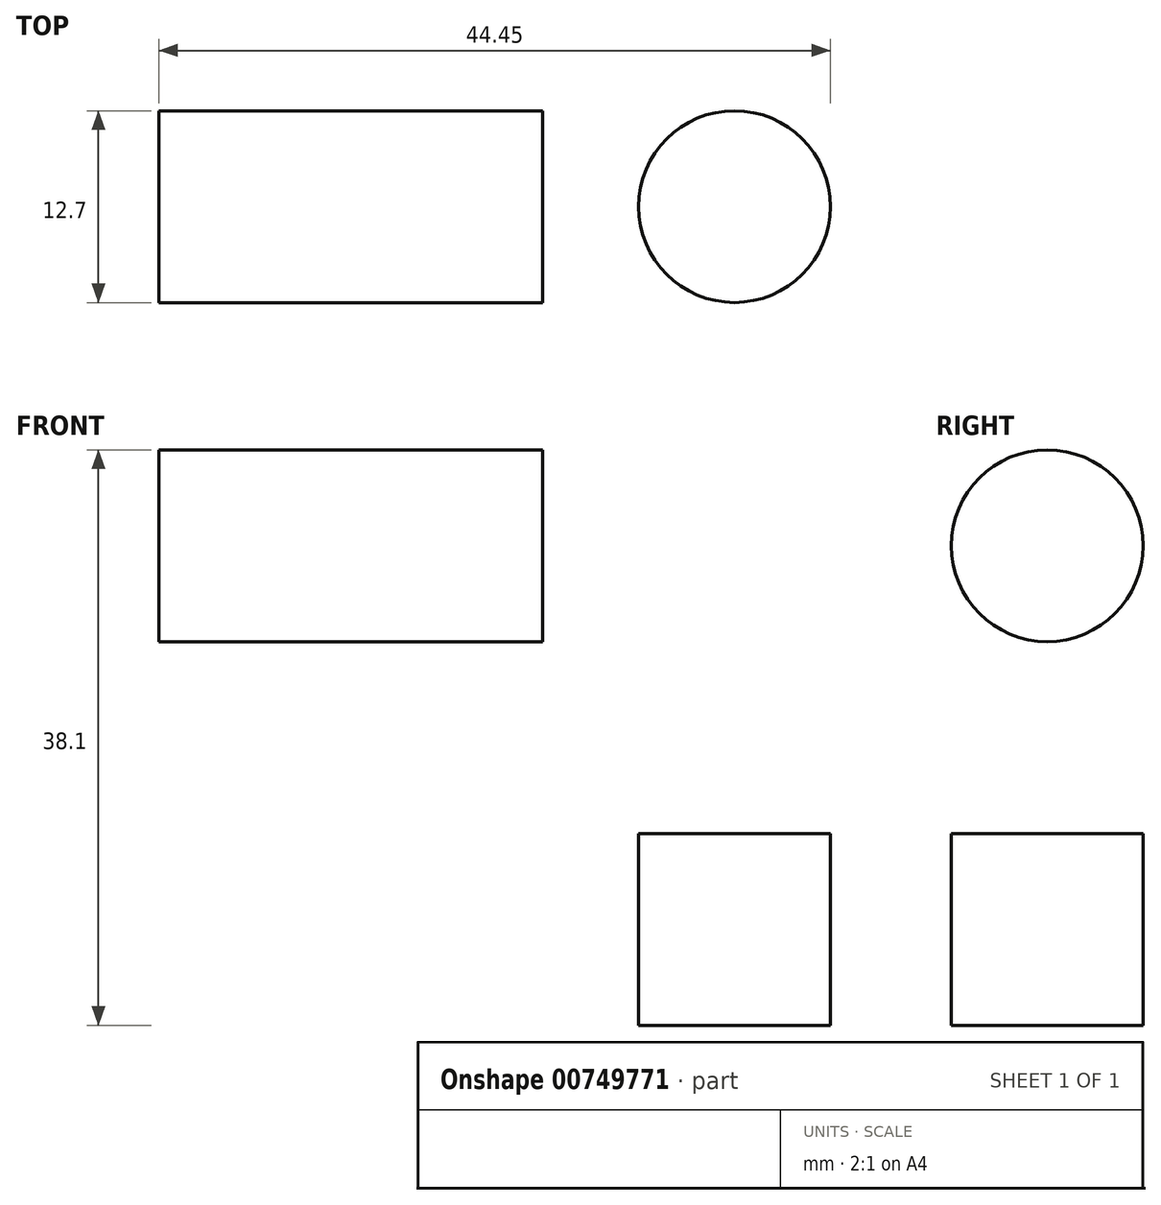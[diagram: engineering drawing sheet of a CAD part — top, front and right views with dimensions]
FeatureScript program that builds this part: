
annotation { "Feature Type Name" : "Feature", "Feature Type Description" : "" }
export const myFeature = defineFeature(function(context is Context, id is Id, definition is map)
    precondition{}
    {
        {
            var Q0;
            Q0=qCreatedBy(makeId("Front.planeOp"),FACE);
            var sketch = newSketch(context, id + "F0", { "sketchPlane" : qUnion([Q0])});
            skLineSegment(sketch, "E0", {"start": v(0, 0) * mm, "end": v(76.2, 0) * mm});
            skLineSegment(sketch, "E1", {"start": v(76.2, 0) * mm, "end": v(76.2, 12.7) * mm});
            skLineSegment(sketch, "E2", {"start": v(76.2, 12.7) * mm, "end": v(50.8, 12.7) * mm});
            skLineSegment(sketch, "E3", {"start": v(50.8, 12.7) * mm, "end": v(50.8, 44.45) * mm});
            skLineSegment(sketch, "E4", {"start": v(50.8, 44.45) * mm, "end": v(25.4, 44.45) * mm});
            skLineSegment(sketch, "E5", {"start": v(25.4, 44.45) * mm, "end": v(25.4, 12.7) * mm});
            skLineSegment(sketch, "E6", {"start": v(25.4, 12.7) * mm, "end": v(0, 12.7) * mm});
            skLineSegment(sketch, "E7", {"start": v(0, 12.7) * mm, "end": v(0, 0) * mm});
            skSolve(sketch);
        }
        {
            var Q0;
            Q0 = qSketchRegion(id + "F0", true);
            extrude(context, id + "F1", {"entities" : qUnion([Q0]), "depth" : 25.4 * mm, "offsetDistance" : 25.4 * mm});
        }
        {
            var Q0;
            Q0=makeQuery(id+"F1.opExtrude","SWEPT_FACE",FACE,{"disambiguationData":[OSD([sQuery(id+"F0.wireOp",EDGE,"E3")])]});
            var sketch = newSketch(context, id + "F2", { "sketchPlane" : qUnion([Q0])});
            skLineSegment(sketch, "E8", {"start": v(-25.4, 31.75) * mm, "end": v(0, 31.75) * mm});
            skCircle(sketch, "E9", {"center": v(-12.7, 31.75) * mm, "radius": 6.35 * mm});
            skArc(sketch, "E10", {"start": v(0, 31.75) * mm, "mid": v(-12.7, 44.42) * mm, "end": v(-25.4, 31.75) * mm});
            skSolve(sketch);
        }
        {
            var Q0;
            {var subQ0=sQuery(id+"F2.wireOp",EDGE,"E9");var subQ1=sQuery(id+"F2.wireOp",EDGE,"E8");var subQ2=makeQuery(id+"F2.imprint","INTERSECT",VERTEX,{"disambiguationData":[OD(0.0)],"derivedFrom":[subQ1,subQ0]});Q0=makeQuery(id+"F2.imprint","IMPRINT",FACE,{"disambiguationData":[TD([[makeQuery(id+"F2.imprint","IMPRINT",EDGE,{"disambiguationData":[TD([[subQ2,-1.0]])],"derivedFrom":subQ1}),-1.0]])]});}
            var Q1;
            {var subQ0=sQuery(id+"F2.wireOp",EDGE,"E9");var subQ1=sQuery(id+"F2.wireOp",EDGE,"E8");var subQ2=makeQuery(id+"F2.imprint","INTERSECT",VERTEX,{"disambiguationData":[OD(0.0)],"derivedFrom":[subQ1,subQ0]});Q1=makeQuery(id+"F2.imprint","IMPRINT",FACE,{"disambiguationData":[TD([[makeQuery(id+"F2.imprint","IMPRINT",EDGE,{"disambiguationData":[TD([[subQ2,-1.0]])],"derivedFrom":subQ1}),1.0]])]});}
            var Q2;
            {var subQ0=sQuery(id+"F2.wireOp",EDGE,"E10");Q2=makeQuery(id+"F2.imprint","IMPRINT",FACE,{"disambiguationData":[TD([[makeQuery(id+"F2.imprint","IMPRINT",EDGE,{"derivedFrom":subQ0}),-1.0]])]});}
            extrude(context, id + "F3", {"entities" : qUnion([Q0, Q1, Q2]), "operationType" : NewBodyOperationType.REMOVE, "endBound" : BoundingType.THROUGH_ALL, "oppositeDirection" : true, "depth" : 25.4 * mm, "offsetDistance" : 25.4 * mm});
        }
        {
            var Q0;
            Q0=makeQuery(id+"F1.opExtrude","SWEPT_FACE",FACE,{"disambiguationData":[OSD([sQuery(id+"F0.wireOp",EDGE,"E2")])]});
            var sketch = newSketch(context, id + "F4", { "sketchPlane" : qUnion([Q0])});
            skLineSegment(sketch, "E11", {"start": v(63.5, 0) * mm, "end": v(63.5, -25.4) * mm});
            skCircle(sketch, "E12", {"center": v(63.5, -12.7) * mm, "radius": 6.35 * mm});
            skArc(sketch, "E13", {"start": v(63.5, -25.4) * mm, "mid": v(76.17, -12.7) * mm, "end": v(63.5, 0) * mm});
            skSolve(sketch);
        }
        {
            var Q0;
            {var subQ0=sQuery(id+"F4.wireOp",EDGE,"E12");var subQ1=sQuery(id+"F4.wireOp",EDGE,"E11");var subQ2=makeQuery(id+"F4.imprint","INTERSECT",VERTEX,{"disambiguationData":[OD(0.0)],"derivedFrom":[subQ1,subQ0]});Q0=makeQuery(id+"F4.imprint","IMPRINT",FACE,{"disambiguationData":[TD([[makeQuery(id+"F4.imprint","IMPRINT",EDGE,{"disambiguationData":[TD([[subQ2,-1.0]])],"derivedFrom":subQ1}),1.0]])]});}
            var Q1;
            {var subQ0=sQuery(id+"F4.wireOp",EDGE,"E12");var subQ1=sQuery(id+"F4.wireOp",EDGE,"E11");var subQ2=makeQuery(id+"F4.imprint","INTERSECT",VERTEX,{"disambiguationData":[OD(0.0)],"derivedFrom":[subQ1,subQ0]});Q1=makeQuery(id+"F4.imprint","IMPRINT",FACE,{"disambiguationData":[TD([[makeQuery(id+"F4.imprint","IMPRINT",EDGE,{"disambiguationData":[TD([[subQ2,-1.0]])],"derivedFrom":subQ1}),-1.0]])]});}
            var Q2;
            {var subQ0=sQuery(id+"F4.wireOp",EDGE,"E13");Q2=makeQuery(id+"F4.imprint","IMPRINT",FACE,{"disambiguationData":[TD([[makeQuery(id+"F4.imprint","IMPRINT",EDGE,{"derivedFrom":subQ0}),-1.0]])]});}
            extrude(context, id + "F5", {"entities" : qUnion([Q0, Q1, Q2]), "operationType" : NewBodyOperationType.REMOVE, "endBound" : BoundingType.THROUGH_ALL, "oppositeDirection" : true, "depth" : 25.4 * mm, "offsetDistance" : 25.4 * mm});
        }
        {
            var Q0;
            Q0=makeQuery(id+"F1.opExtrude","SWEPT_FACE",FACE,{"disambiguationData":[OSD([sQuery(id+"F0.wireOp",EDGE,"E6")])]});
            var sketch = newSketch(context, id + "F6", { "sketchPlane" : qUnion([Q0])});
            skLineSegment(sketch, "E14", {"start": v(12.7, 0) * mm, "end": v(12.7, -25.4) * mm});
            skCircle(sketch, "E15", {"center": v(12.7, -12.7) * mm, "radius": 6.35 * mm});
            skArc(sketch, "E16", {"start": v(12.7, 0) * mm, "mid": v(0.53, -12.7) * mm, "end": v(12.7, -25.4) * mm});
            skSolve(sketch);
        }
        {
            var Q0;
            {var subQ0=sQuery(id+"F6.wireOp",EDGE,"E15");var subQ1=sQuery(id+"F6.wireOp",EDGE,"E14");var subQ2=makeQuery(id+"F6.imprint","INTERSECT",VERTEX,{"disambiguationData":[OD(0.0)],"derivedFrom":[subQ1,subQ0]});Q0=makeQuery(id+"F6.imprint","IMPRINT",FACE,{"disambiguationData":[TD([[makeQuery(id+"F6.imprint","IMPRINT",EDGE,{"disambiguationData":[TD([[subQ2,-1.0]])],"derivedFrom":subQ1}),1.0]])]});}
            var Q1;
            {var subQ0=sQuery(id+"F6.wireOp",EDGE,"E15");var subQ1=sQuery(id+"F6.wireOp",EDGE,"E14");var subQ2=makeQuery(id+"F6.imprint","INTERSECT",VERTEX,{"disambiguationData":[OD(0.0)],"derivedFrom":[subQ1,subQ0]});Q1=makeQuery(id+"F6.imprint","IMPRINT",FACE,{"disambiguationData":[TD([[makeQuery(id+"F6.imprint","IMPRINT",EDGE,{"disambiguationData":[TD([[subQ2,-1.0]])],"derivedFrom":subQ1}),-1.0]])]});}
            var Q2;
            {var subQ0=sQuery(id+"F6.wireOp",EDGE,"E16");Q2=makeQuery(id+"F6.imprint","IMPRINT",FACE,{"disambiguationData":[TD([[makeQuery(id+"F6.imprint","IMPRINT",EDGE,{"derivedFrom":subQ0}),-1.0]])]});}
            extrude(context, id + "F7", {"entities" : qUnion([Q0, Q1, Q2]), "operationType" : NewBodyOperationType.REMOVE, "endBound" : BoundingType.THROUGH_ALL, "oppositeDirection" : true, "depth" : 25.4 * mm, "offsetDistance" : 25.4 * mm});
        }
    });
